# Revit family: Walkway_KattsafeUSA_Guardrail2Sides_Levelled
name_source: partatom
category: Specialty Equipment
units: mm (PartAtom-declared; Revit-internal decimal feet)

## family parameters
Classification Number = 23.13.41.19
Cut with Voids When Loaded = No
Enable Cutting in Views = No
Maintain Annotation Orientation = No
Part Type = Normal
Room Calculation Point = No
Round Connector Dimension = Use Diameter
Shared = No

## types (1)
- GW7
    Assembly Code = E1090100
    Default Elevation = 0' - 0"
    Description = Kattsafe guardrail systems are the preferred method of safe access across roofs and areas close to a fall edge. The system requires no specialist PPE, personnel or training to safely prevent a fall with a walkway to designate a safe path of access across the roof surface.
    ElementType = Roof Walkway
    Export Type to IFC As = IfcBuildingElementProxy
    GuardrailHeight = 3' - 3"
    HandrailAngledOffsetHeight = -0' - 2"
    HandrailClosureAngledOffsetHeight = -1' - 9"
    IfcExportAs = IfcBuildingElementProxy
    IfcExportType = USERDEFINED
    Manufacturer = Kattsafe®
    ManufacturerOverallHeight = 3' - 5"
    ManufacturerOverallHeightCalc = 3' - 5"
    ManufacturerOverallWidth = 4' - 7"
    ManufacturerSpecCode = GW7
    ManufacturerURLProductSpecific = https://kattsafe.com
    Material = Aluminum_Kattsafe_Satin
    Model = GW7
    ModifiedIssue = 20250703 $
    PostsHeight = 3' - 3 1/2"
    PostsMaxSpacingLength = 6' - 6 1/2"
    Type Comments = Walkway - 2 Sides - Guardrail - Levelled
    Type IFC Predefined Type = USERDEFINED
    URL = https://kattsafe.com
    Uniclass2015Code = Pr_40_70_75_96
    Uniclass2015Title = Working platforms
    Uniclass2015Version = Products v1.35
    WalkwayMaterial = Aluminum_Kattsafe_Mesh_Walkway
    WalkwayWidth = 1' - 11 1/2"

## geometry (parser evidence)
native form markers: Sweep x14
no freeform markers — native parametric forms only
